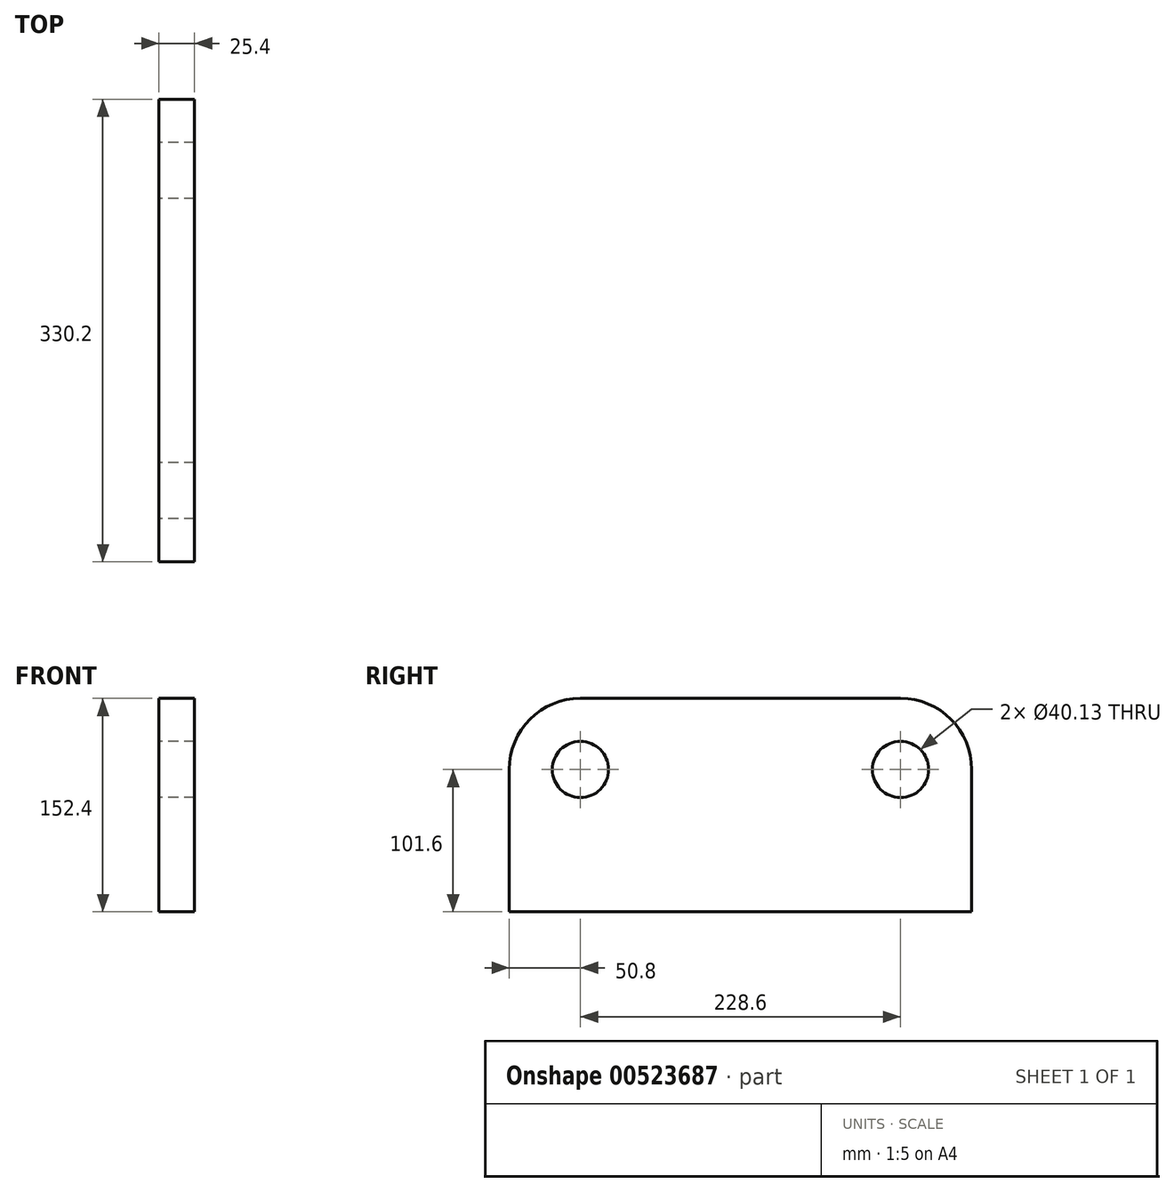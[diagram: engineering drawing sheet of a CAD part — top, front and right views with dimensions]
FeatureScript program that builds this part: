
annotation { "Feature Type Name" : "Feature", "Feature Type Description" : "" }
export const myFeature = defineFeature(function(context is Context, id is Id, definition is map)
    precondition{}
    {
        {
            var Q0;
            Q0=qCreatedBy(makeId("Right.planeOp"),FACE);
            var sketch = newSketch(context, id + "F0", { "sketchPlane" : qUnion([Q0])});
            skLineSegment(sketch, "E0.bottom", {"start": v(50.8, 0) * mm, "end": v(279.4, 0) * mm});
            skLineSegment(sketch, "E0.top", {"start": v(0, -152.4) * mm, "end": v(330.2, -152.4) * mm});
            skLineSegment(sketch, "E0.left", {"start": v(0, -50.8) * mm, "end": v(0, -152.4) * mm});
            skLineSegment(sketch, "E0.right", {"start": v(330.2, -50.8) * mm, "end": v(330.2, -152.4) * mm});
            skCircle(sketch, "E1", {"center": v(50.8, -50.8) * mm, "radius": 20.07 * mm});
            skCircle(sketch, "E2", {"center": v(279.4, -50.8) * mm, "radius": 20.07 * mm});
            skPoint(sketch, "E3.visualSharp", {"position": v(0, 0) * mm});
            skArc(sketch, "E3.filletArc", {"start": v(50.8, 0) * mm, "mid": v(14.88, -14.88) * mm, "end": v(0, -50.8) * mm});
            skPoint(sketch, "E4.visualSharp", {"position": v(330.2, 0) * mm});
            skArc(sketch, "E4.filletArc", {"start": v(330.2, -50.8) * mm, "mid": v(315.32, -14.88) * mm, "end": v(279.4, 0) * mm});
            skSolve(sketch);
        }
        {
            var Q0;
            Q0=makeQuery(id+"F0.imprint","IMPRINT",FACE,{"disambiguationData":[TD([[makeQuery(id+"F0.imprint","IMPRINT",EDGE,{"derivedFrom":sQuery(id+"F0.wireOp",EDGE,"E0.bottom")}),-1.0]])]});
            extrude(context, id + "F1", {"entities" : qUnion([Q0]), "depth" : 25.4 * mm, "offsetDistance" : 25.4 * mm});
        }
    });
